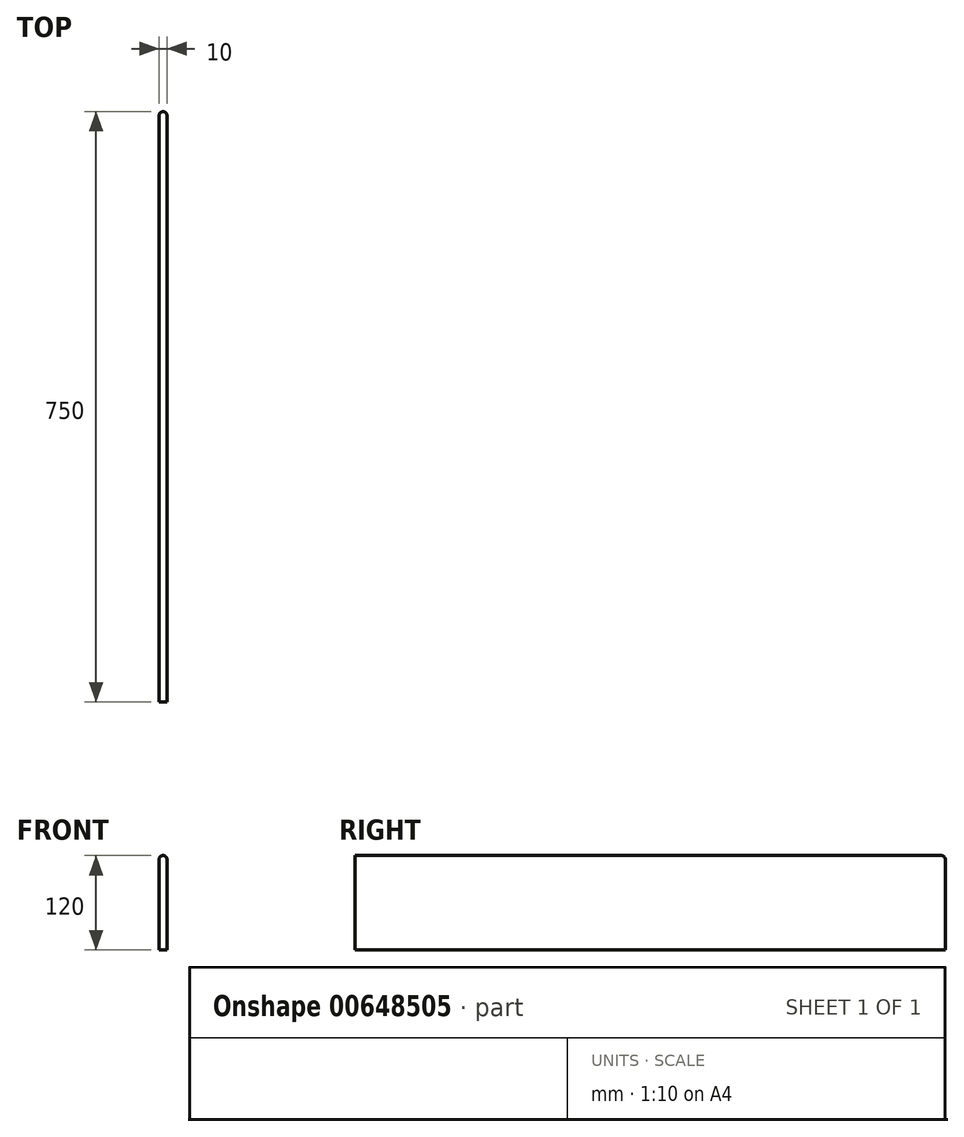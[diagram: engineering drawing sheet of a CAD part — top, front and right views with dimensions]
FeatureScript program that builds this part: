
annotation { "Feature Type Name" : "Feature", "Feature Type Description" : "" }
export const myFeature = defineFeature(function(context is Context, id is Id, definition is map)
    precondition{}
    {
        {
            var Q0;
            Q0=qCreatedBy(makeId("Right.planeOp"),FACE);
            var sketch = newSketch(context, id + "F0", { "sketchPlane" : qUnion([Q0])});
            skLineSegment(sketch, "E0.bottom", {"start": v(375, -60) * mm, "end": v(-375, -60) * mm});
            skLineSegment(sketch, "E0.top", {"start": v(375, 60) * mm, "end": v(-375, 60) * mm});
            skLineSegment(sketch, "E0.left", {"start": v(375, -60) * mm, "end": v(375, 60) * mm});
            skLineSegment(sketch, "E0.right", {"start": v(-375, -60) * mm, "end": v(-375, 60) * mm});
            skPoint(sketch, "E0.middle", {"position": v(0, 0) * mm});
            skSolve(sketch);
        }
        {
            var Q0;
            Q0 = qSketchRegion(id + "F0", true);
            extrude(context, id + "F1", {"entities" : qUnion([Q0]), "depth" : 10 * mm, "offsetDistance" : 25 * mm});
        }
        {
            var Q0;
            Q0=makeQuery(id+"F1.opExtrude","CAP_EDGE",EDGE,{"disambiguationData":[OSD([sQuery(id+"F0.wireOp",EDGE,"E0.left")])],"isStart":false});
            var Q1;
            Q1=makeQuery(id+"F1.opExtrude","SWEPT_EDGE",EDGE,{"disambiguationData":[OSD([sQuery(id+"F0.wireOp",EDGE,"E0.top"),sQuery(id+"F0.wireOp",EDGE,"E0.left")])]});
            var Q2;
            Q2=makeQuery(id+"F1.opExtrude","CAP_EDGE",EDGE,{"disambiguationData":[OSD([sQuery(id+"F0.wireOp",EDGE,"E0.left")])],"isStart":true});
            var Q3;
            Q3=makeQuery(id+"F1.opExtrude","CAP_EDGE",EDGE,{"disambiguationData":[OSD([sQuery(id+"F0.wireOp",EDGE,"E0.top")])],"isStart":true});
            var Q4;
            Q4=makeQuery(id+"F1.opExtrude","CAP_EDGE",EDGE,{"disambiguationData":[OSD([sQuery(id+"F0.wireOp",EDGE,"E0.top")])],"isStart":false});
            fillet(context, id + "F2", {"entities" : qUnion([Q0, Q1, Q2, Q3, Q4]), "radius" : 5 * mm, "tangentPropagation" : true, "allowEdgeOverflow" : false});
        }
    });
